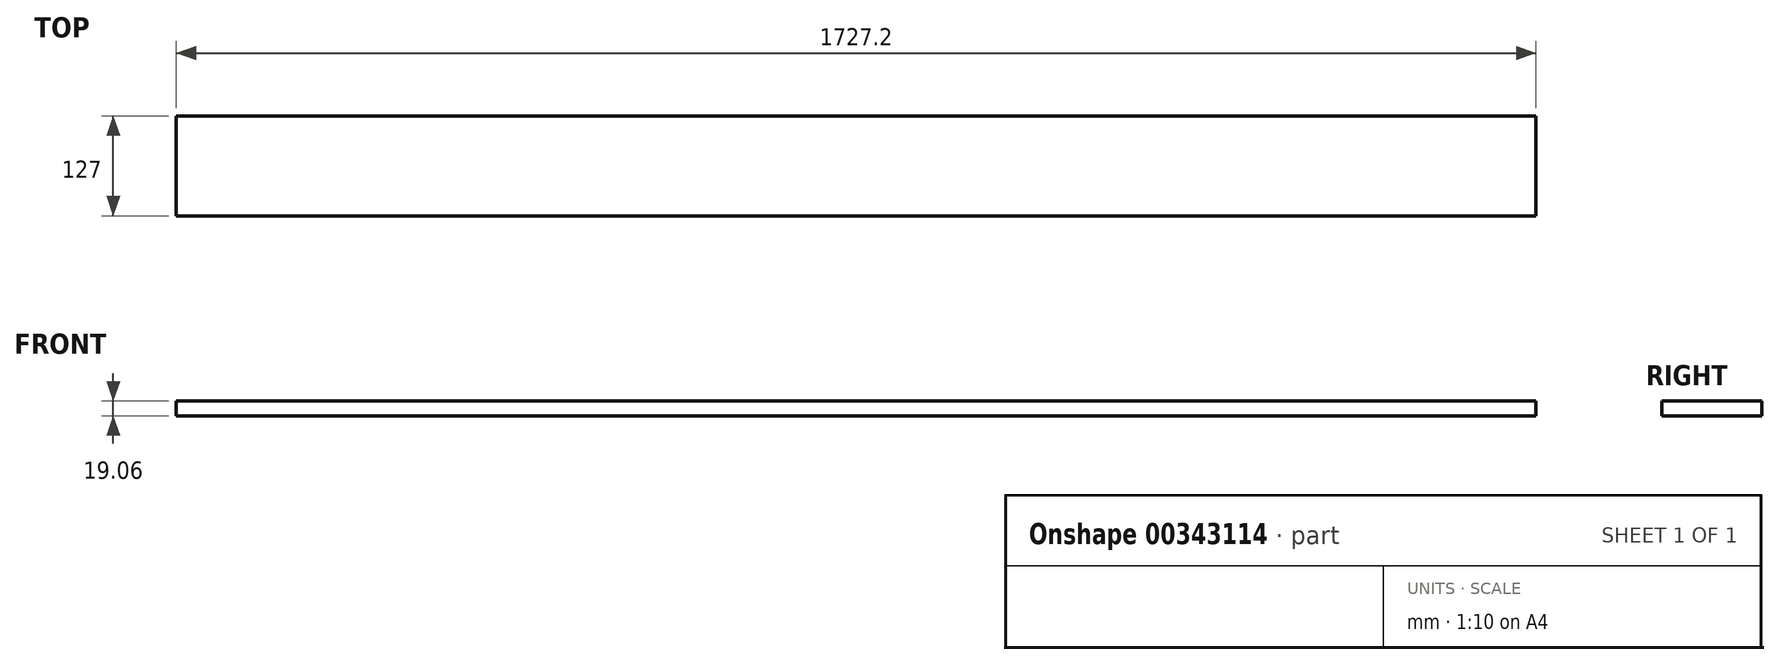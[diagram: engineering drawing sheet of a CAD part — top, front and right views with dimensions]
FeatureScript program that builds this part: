
annotation { "Feature Type Name" : "Feature", "Feature Type Description" : "" }
export const myFeature = defineFeature(function(context is Context, id is Id, definition is map)
    precondition{}
    {
        {
            var Q0;
            Q0=qCreatedBy(makeId("Right.planeOp"),FACE);
            var sketch = newSketch(context, id + "F0", { "sketchPlane" : qUnion([Q0])});
            skLineSegment(sketch, "E0.bottom", {"start": v(-63.5, 9.53) * mm, "end": v(63.5, 9.53) * mm});
            skLineSegment(sketch, "E0.top", {"start": v(-63.5, -9.52) * mm, "end": v(63.5, -9.52) * mm});
            skLineSegment(sketch, "E0.left", {"start": v(-63.5, 9.53) * mm, "end": v(-63.5, -9.52) * mm});
            skLineSegment(sketch, "E0.right", {"start": v(63.5, 9.53) * mm, "end": v(63.5, -9.52) * mm});
            skSolve(sketch);
        }
        {
            var Q0;
            Q0=makeQuery(id+"F0.imprint","IMPRINT",FACE,{"disambiguationData":[TD([[makeQuery(id+"F0.imprint","IMPRINT",EDGE,{"derivedFrom":sQuery(id+"F0.wireOp",EDGE,"E0.bottom")}),-1.0]])]});
            extrude(context, id + "F1", {"entities" : qUnion([Q0]), "endBound" : BoundingType.SYMMETRIC, "depth" : 1727.2 * mm});
        }
    });
